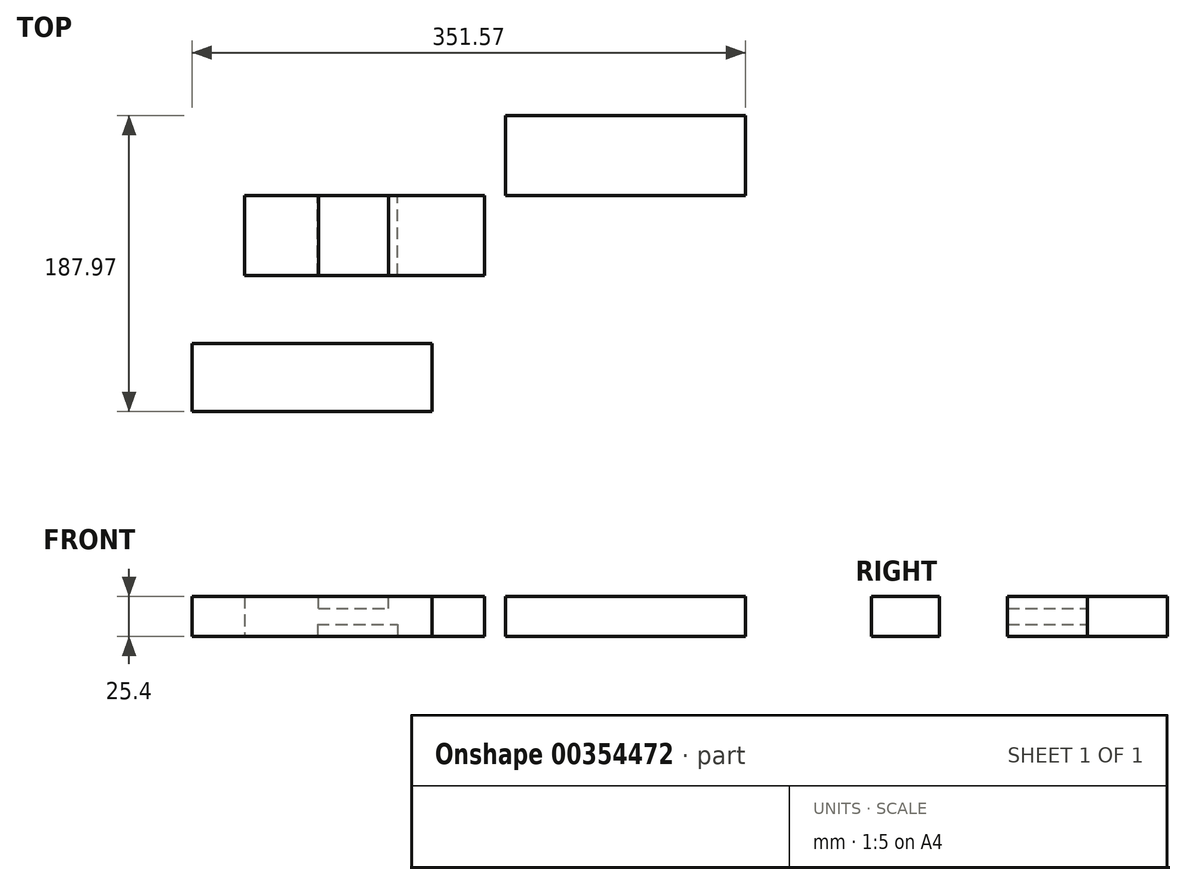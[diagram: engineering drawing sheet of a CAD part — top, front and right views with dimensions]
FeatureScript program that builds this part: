
annotation { "Feature Type Name" : "Feature", "Feature Type Description" : "" }
export const myFeature = defineFeature(function(context is Context, id is Id, definition is map)
    precondition{}
    {
        {
            var Q0;
            Q0=qCreatedBy(makeId("Top.planeOp"),FACE);
            var sketch = newSketch(context, id + "F0", { "sketchPlane" : qUnion([Q0])});
            skLineSegment(sketch, "E0.bottom", {"start": v(-111.53, 0) * mm, "end": v(40.87, 0) * mm});
            skLineSegment(sketch, "E0.top", {"start": v(-111.53, -50.8) * mm, "end": v(40.87, -50.8) * mm});
            skLineSegment(sketch, "E0.left", {"start": v(-111.53, 0) * mm, "end": v(-111.53, -50.8) * mm});
            skLineSegment(sketch, "E0.right", {"start": v(40.87, 0) * mm, "end": v(40.87, -50.8) * mm});
            skSolve(sketch);
        }
        {
            var Q0;
            Q0=makeQuery(id+"F0.imprint","IMPRINT",FACE,{"disambiguationData":[TD([[makeQuery(id+"F0.imprint","IMPRINT",EDGE,{"derivedFrom":sQuery(id+"F0.wireOp",EDGE,"E0.bottom")}),-1.0]])]});
            extrude(context, id + "F1", {"entities" : qUnion([Q0]), "depth" : 25.4 * mm});
        }
        {
            var Q0;
            Q0=makeQuery(id+"F1.opExtrude","CAP_FACE",FACE,{"disambiguationData":[OSD([sQuery(id+"F0.wireOp",EDGE,"E0.bottom"),sQuery(id+"F0.wireOp",EDGE,"E0.top"),sQuery(id+"F0.wireOp",EDGE,"E0.left"),sQuery(id+"F0.wireOp",EDGE,"E0.right")])],"isStart":false});
            var sketch = newSketch(context, id + "F2", { "sketchPlane" : qUnion([Q0])});
            skLineSegment(sketch, "E1", {"start": v(-64.62, -50.8) * mm, "end": v(-64.62, 0) * mm});
            skLineSegment(sketch, "E2", {"start": v(-64.62, -50.8) * mm, "end": v(-19.93, -50.8) * mm});
            skLineSegment(sketch, "E3", {"start": v(-19.93, -50.8) * mm, "end": v(-19.93, 0) * mm});
            skLineSegment(sketch, "E4", {"start": v(-19.93, 0) * mm, "end": v(-64.62, 0) * mm});
            skSolve(sketch);
        }
        {
            var Q0;
            Q0=makeQuery(id+"F2.imprint","IMPRINT",FACE,{"disambiguationData":[TD([[makeQuery(id+"F2.imprint","IMPRINT",EDGE,{"derivedFrom":sQuery(id+"F2.wireOp",EDGE,"E1")}),-1.0]])]});
            extrude(context, id + "F3", {"entities" : qUnion([Q0]), "operationType" : NewBodyOperationType.REMOVE, "oppositeDirection" : true, "depth" : 7.62 * mm});
        }
        {
            var Q0;
            Q0=qCreatedBy(makeId("Top.planeOp"),FACE);
            var sketch = newSketch(context, id + "F4", { "sketchPlane" : qUnion([Q0])});
            skLineSegment(sketch, "E5.bottom", {"start": v(-144.87, -93.99) * mm, "end": v(7.53, -93.99) * mm});
            skLineSegment(sketch, "E5.top", {"start": v(-144.87, -137.17) * mm, "end": v(7.53, -137.17) * mm});
            skLineSegment(sketch, "E5.left", {"start": v(-144.87, -93.99) * mm, "end": v(-144.87, -137.17) * mm});
            skLineSegment(sketch, "E5.right", {"start": v(7.53, -93.99) * mm, "end": v(7.53, -137.17) * mm});
            skPoint(sketch, "E5.middle", {"position": v(-68.67, -115.58) * mm});
            skSolve(sketch);
        }
        {
            var Q0;
            Q0=makeQuery(id+"F4.imprint","IMPRINT",FACE,{"disambiguationData":[TD([[makeQuery(id+"F4.imprint","IMPRINT",EDGE,{"derivedFrom":sQuery(id+"F4.wireOp",EDGE,"E5.bottom")}),-1.0]])]});
            extrude(context, id + "F5", {"entities" : qUnion([Q0]), "depth" : 25.4 * mm});
        }
        {
            var Q0;
            Q0=makeQuery(id+"F1.opExtrude","CAP_FACE",FACE,{"disambiguationData":[OSD([sQuery(id+"F0.wireOp",EDGE,"E0.bottom"),sQuery(id+"F0.wireOp",EDGE,"E0.top"),sQuery(id+"F0.wireOp",EDGE,"E0.left"),sQuery(id+"F0.wireOp",EDGE,"E0.right")])],"isStart":true});
            var sketch = newSketch(context, id + "F6", { "sketchPlane" : qUnion([Q0])});
            skLineSegment(sketch, "E6.bottom", {"start": v(-65.2, 50.8) * mm, "end": v(-14.4, 50.8) * mm});
            skLineSegment(sketch, "E6.top", {"start": v(-65.2, 0) * mm, "end": v(-14.4, 0) * mm});
            skLineSegment(sketch, "E6.left", {"start": v(-65.2, 50.8) * mm, "end": v(-65.2, 0) * mm});
            skLineSegment(sketch, "E6.right", {"start": v(-14.4, 50.8) * mm, "end": v(-14.4, 0) * mm});
            skSolve(sketch);
        }
        {
            var Q0;
            Q0=makeQuery(id+"F6.imprint","IMPRINT",FACE,{"disambiguationData":[TD([[makeQuery(id+"F6.imprint","IMPRINT",EDGE,{"derivedFrom":sQuery(id+"F6.wireOp",EDGE,"E6.bottom")}),-1.0]])]});
            extrude(context, id + "F7", {"entities" : qUnion([Q0]), "operationType" : NewBodyOperationType.REMOVE, "oppositeDirection" : true, "depth" : 7.62 * mm});
        }
        {
            var Q0;
            Q0=qCreatedBy(makeId("Top.planeOp"),FACE);
            var sketch = newSketch(context, id + "F8", { "sketchPlane" : qUnion([Q0])});
            skLineSegment(sketch, "E7.bottom", {"start": v(54.3, 50.8) * mm, "end": v(206.7, 50.8) * mm});
            skLineSegment(sketch, "E7.top", {"start": v(54.3, 0) * mm, "end": v(206.7, 0) * mm});
            skLineSegment(sketch, "E7.left", {"start": v(54.3, 50.8) * mm, "end": v(54.3, 0) * mm});
            skLineSegment(sketch, "E7.right", {"start": v(206.7, 50.8) * mm, "end": v(206.7, 0) * mm});
            skSolve(sketch);
        }
        {
            var Q0;
            Q0 = qSketchRegion(id + "F8", true);
            extrude(context, id + "F9", {"entities" : qUnion([Q0]), "depth" : 25.4 * mm});
        }
    });
